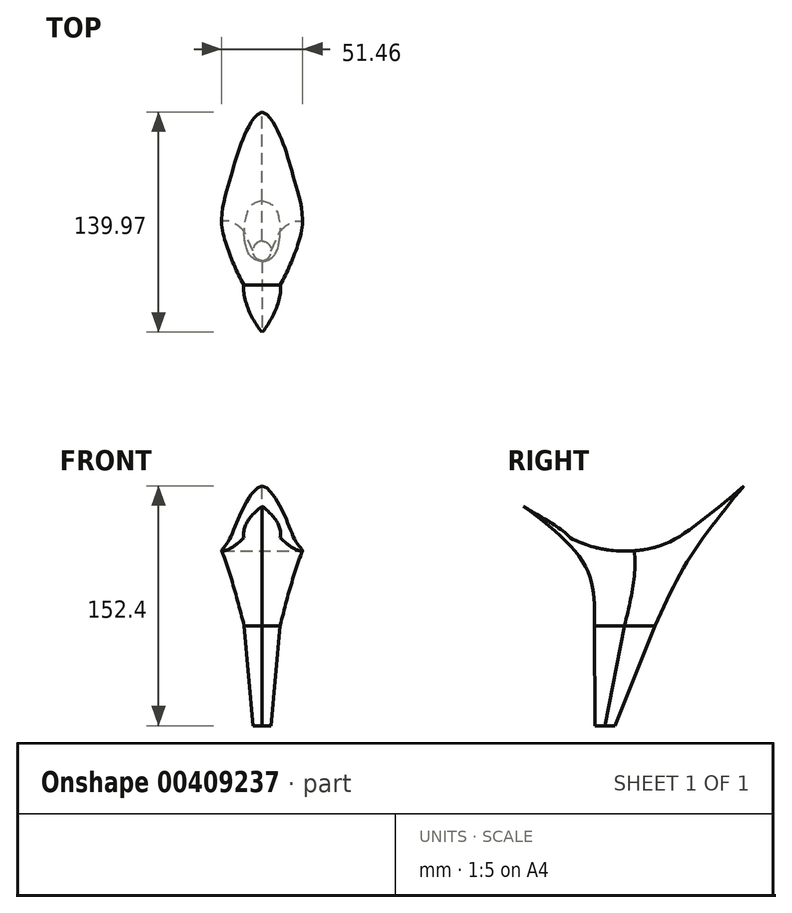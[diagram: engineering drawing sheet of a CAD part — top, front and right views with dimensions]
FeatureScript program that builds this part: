
annotation { "Feature Type Name" : "Feature", "Feature Type Description" : "" }
export const myFeature = defineFeature(function(context is Context, id is Id, definition is map)
    precondition{}
    {
        {
            var Q0;
            Q0=qCreatedBy(makeId("Top.planeOp"),FACE);
            var sketch = newSketch(context, id + "F0", { "sketchPlane" : qUnion([Q0])});
            skCircle(sketch, "E0", {"center": v(0, 0) * mm, "radius": 5.72 * mm, "construction": true});
            skFitSpline(sketch, "E1", {"points": [v(0, 6.35) * mm, v(-4.03, 4.38) * mm, v(-5.72, 0) * mm], "startDerivative": vector(-10.05, -1.39) * mm, "endDerivative": vector(-0.35, -12.15) * mm});
            skCircle(sketch, "E2", {"center": v(0, 0) * mm, "radius": 6.35 * mm, "construction": true});
            skFitSpline(sketch, "E3.MirrorCS", {"points": [v(0, 6.35) * mm, v(4.03, 4.38) * mm, v(5.72, 0) * mm], "startDerivative": vector(10.05, -1.39) * mm, "endDerivative": vector(0.35, -12.15) * mm});
            skFitSpline(sketch, "E4.MirrorCS", {"points": [v(0, -6.35) * mm, v(-4.03, -4.38) * mm, v(-5.72, 0) * mm], "startDerivative": vector(-10.05, 1.39) * mm, "endDerivative": vector(-0.35, 12.15) * mm});
            skFitSpline(sketch, "E5.MirrorCS", {"points": [v(0, -6.35) * mm, v(4.03, -4.38) * mm, v(5.72, 0) * mm], "startDerivative": vector(10.05, 1.39) * mm, "endDerivative": vector(0.35, 12.15) * mm});
            skSolve(sketch);
        }
        {
            var Q0;
            Q0=qCreatedBy(makeId("Top.planeOp"),FACE);
            cPlane(context, id + "F1", {"entities" : qUnion([Q0]), "cplaneType" : CPlaneType.OFFSET, "offset" : 63.5 * mm, "width" : 152.4 * mm, "height" : 152.4 * mm});
        }
        {
            var Q0;
            Q0=qCreatedBy(id+"F1.planeOp",FACE);
            var sketch = newSketch(context, id + "F2", { "sketchPlane" : qUnion([Q0])});
            skCircle(sketch, "E6", {"center": v(0, 12.7) * mm, "radius": 11.43 * mm, "construction": true});
            skCircle(sketch, "E7", {"center": v(0, 12.7) * mm, "radius": 19.05 * mm, "construction": true});
            skFitSpline(sketch, "E8", {"points": [v(0, 31.75) * mm, v(-8.42, 26.77) * mm, v(-11.43, 12.5) * mm], "startDerivative": vector(-23.54, -2.2) * mm, "endDerivative": vector(-0.5, -26.09) * mm});
            skFitSpline(sketch, "E9.MirrorCS", {"points": [v(0, 31.75) * mm, v(8.42, 26.77) * mm, v(11.43, 12.5) * mm], "startDerivative": vector(23.54, -2.2) * mm, "endDerivative": vector(0.5, -26.09) * mm});
            skLineSegment(sketch, "E10", {"start": v(-11.43, 12.5) * mm, "end": v(11.43, 12.5) * mm, "construction": true});
            skFitSpline(sketch, "E11.MirrorCS", {"points": [v(0, -6.74) * mm, v(-8.42, -1.77) * mm, v(-11.43, 12.5) * mm], "startDerivative": vector(-23.54, 2.2) * mm, "endDerivative": vector(-0.5, 26.09) * mm});
            skFitSpline(sketch, "E12.MirrorCS", {"points": [v(0, -6.74) * mm, v(8.42, -1.77) * mm, v(11.43, 12.5) * mm], "startDerivative": vector(23.54, 2.2) * mm, "endDerivative": vector(0.5, 26.09) * mm});
            skPoint(sketch, "E13.0", {"position": v(0, 0) * mm});
            skSolve(sketch);
        }
        {
            var Q0;
            Q0=makeQuery(id+"F0.imprint","IMPRINT",FACE,{"disambiguationData":[TD([[makeQuery(id+"F0.imprint","IMPRINT",EDGE,{"derivedFrom":sQuery(id+"F0.wireOp",EDGE,"E1")}),1.0]])]});
            var Q1;
            Q1=makeQuery(id+"F2.imprint","IMPRINT",FACE,{"disambiguationData":[TD([[makeQuery(id+"F2.imprint","IMPRINT",EDGE,{"derivedFrom":sQuery(id+"F2.wireOp",EDGE,"E8")}),1.0]])]});
            loft(context, id + "F3", {"sheetProfilesArray" : [{ "sheetProfileEntities" : qUnion([Q0]) }, { "sheetProfileEntities" : qUnion([Q1]) }]});
        }
        {
            var Q0;
            Q0=qCreatedBy(id+"F1.planeOp",FACE);
            cPlane(context, id + "F4", {"entities" : qUnion([Q0]), "cplaneType" : CPlaneType.OFFSET, "offset" : 38.1 * mm, "width" : 152.4 * mm, "height" : 152.4 * mm});
        }
        {
            var Q0;
            Q0=qCreatedBy(id+"F4.planeOp",FACE);
            var sketch = newSketch(context, id + "F5", { "sketchPlane" : qUnion([Q0])});
            skPoint(sketch, "E14.0", {"position": v(0, 0) * mm});
            skCircle(sketch, "E15", {"center": v(0, 19.05) * mm, "radius": 22.23 * mm, "construction": true});
            skCircle(sketch, "E16", {"center": v(0, 19.05) * mm, "radius": 31.75 * mm, "construction": true});
            skFitSpline(sketch, "E17", {"points": [v(0, 50.8) * mm, v(-14.15, 42.4) * mm, v(-22.22, 19.05) * mm], "startDerivative": vector(-46.14, -5.08) * mm, "endDerivative": vector(-0.3, -42.83) * mm});
            skLineSegment(sketch, "E18", {"start": v(-22.22, 19.05) * mm, "end": v(22.22, 19.05) * mm, "construction": true});
            skFitSpline(sketch, "E19.MirrorCS", {"points": [v(0, 50.8) * mm, v(14.15, 42.4) * mm, v(22.22, 19.05) * mm], "startDerivative": vector(46.14, -5.08) * mm, "endDerivative": vector(0.3, -42.83) * mm});
            skLineSegment(sketch, "E20.MirrorCS", {"start": v(22.22, 19.05) * mm, "end": v(-22.22, 19.05) * mm, "construction": true});
            skFitSpline(sketch, "E21.MirrorCS", {"points": [v(0, -12.7) * mm, v(-14.15, -4.3) * mm, v(-22.22, 19.05) * mm], "startDerivative": vector(-46.14, 5.08) * mm, "endDerivative": vector(-0.3, 42.83) * mm});
            skFitSpline(sketch, "E22.MirrorCS", {"points": [v(0, -12.7) * mm, v(14.15, -4.3) * mm, v(22.22, 19.05) * mm], "startDerivative": vector(46.14, 5.08) * mm, "endDerivative": vector(0.3, 42.83) * mm});
            skSolve(sketch);
        }
        {
            var Q0;
            Q0=qCreatedBy(id+"F4.planeOp",FACE);
            cPlane(context, id + "F6", {"entities" : qUnion([Q0]), "cplaneType" : CPlaneType.OFFSET, "offset" : 50.8 * mm, "width" : 152.4 * mm, "height" : 152.4 * mm});
        }
        {
            var Q0;
            Q0=qCreatedBy(id+"F6.planeOp",FACE);
            var sketch = newSketch(context, id + "F7", { "sketchPlane" : qUnion([Q0])});
            skPoint(sketch, "E23.0", {"position": v(0, 0) * mm});
            skCircle(sketch, "E24", {"center": v(0, 8.9) * mm, "radius": 44.45 * mm, "construction": true});
            skCircle(sketch, "E25", {"center": v(0, 8.9) * mm, "radius": 79.38 * mm, "construction": true});
            skFitSpline(sketch, "E26", {"points": [v(0, 88.26) * mm, v(-27.3, 62.72) * mm, v(-44.45, 8.9) * mm], "startDerivative": vector(-70.11, -4.65) * mm, "endDerivative": vector(4.08, -70.7) * mm});
            skLineSegment(sketch, "E27", {"start": v(-44.45, 8.9) * mm, "end": v(44.45, 8.9) * mm, "construction": true});
            skFitSpline(sketch, "E28.MirrorCS", {"points": [v(0, 88.26) * mm, v(27.3, 62.72) * mm, v(44.45, 8.9) * mm], "startDerivative": vector(70.11, -4.65) * mm, "endDerivative": vector(-4.08, -70.7) * mm});
            skFitSpline(sketch, "E29.MirrorCS", {"points": [v(0, -70.48) * mm, v(27.3, -44.94) * mm, v(44.45, 8.9) * mm], "startDerivative": vector(70.11, 4.65) * mm, "endDerivative": vector(-4.08, 70.7) * mm});
            skFitSpline(sketch, "E30.MirrorCS", {"points": [v(0, -70.48) * mm, v(-27.3, -44.94) * mm, v(-44.45, 8.9) * mm], "startDerivative": vector(-70.11, 4.65) * mm, "endDerivative": vector(4.08, 70.7) * mm});
            skSolve(sketch);
        }
        {
            var Q1;
            Q1=makeQuery(id+"F3.opLoft","CAP_FACE",FACE,{"disambiguationData":[OSD([makeQuery(id+"F2.imprint","IMPRINT",FACE,{"disambiguationData":[TD([[makeQuery(id+"F2.imprint","IMPRINT",EDGE,{"derivedFrom":sQuery(id+"F2.wireOp",EDGE,"E8")}),1.0]])]})])],"isStart":true});
            var Q2;
            Q2=makeQuery(id+"F5.imprint","IMPRINT",FACE,{"disambiguationData":[TD([[makeQuery(id+"F5.imprint","IMPRINT",EDGE,{"derivedFrom":sQuery(id+"F5.wireOp",EDGE,"E17")}),1.0]])]});
            var Q3;
            Q3=makeQuery(id+"F7.imprint","IMPRINT",FACE,{"disambiguationData":[TD([[makeQuery(id+"F7.imprint","IMPRINT",EDGE,{"derivedFrom":sQuery(id+"F7.wireOp",EDGE,"E26")}),1.0]])]});
            loft(context, id + "F8", {"sheetProfilesArray" : [{ "sheetProfileEntities" : qUnion([Q1]) }, { "sheetProfileEntities" : qUnion([Q2]) }, { "sheetProfileEntities" : qUnion([Q3]) }]});
        }
        {
            var Q0;
            Q0=qCreatedBy(makeId("Right.planeOp"),FACE);
            var sketch = newSketch(context, id + "F9", { "sketchPlane" : qUnion([Q0])});
            skFitSpline(sketch, "E31", {"points": [v(88.26, 152.4) * mm, v(61.41, 130.28) * mm, v(36.73, 114.88) * mm, v(2.95, 111.52) * mm, v(-33.09, 124.93) * mm], "startDerivative": vector(-132.87, -117.4) * mm, "endDerivative": vector(-161.22, 88.58) * mm});
            skFitSpline(sketch, "E32.0", {"points": [v(-12.7, 101.6) * mm, v(-22.23, 119.6) * mm, v(-46.36, 136) * mm, v(-70.48, 152.4) * mm]});
            skFitSpline(sketch, "E33.0.0", {"points": [v(12.5, 63.5) * mm, v(15.59, 76.45) * mm, v(18.68, 89.4) * mm, v(19.05, 101.6) * mm]});
            skFitSpline(sketch, "E33.0.1", {"points": [v(19.05, 101.6) * mm, v(19.6, 119.6) * mm, v(14.25, 136) * mm, v(8.9, 152.4) * mm]});
            skFitSpline(sketch, "E33.0.2", {"points": [v(8.9, 152.4) * mm, v(-17.57, 152.4) * mm, v(-44.03, 152.4) * mm, v(-70.48, 152.4) * mm]});
            skFitSpline(sketch, "E33.0.3", {"points": [v(-70.48, 152.4) * mm, v(-46.36, 136) * mm, v(-22.23, 119.6) * mm, v(-12.7, 101.6) * mm]});
            skFitSpline(sketch, "E34.0.2", {"points": [v(88.26, 152.4) * mm, v(61.8, 152.4) * mm, v(35.35, 152.4) * mm, v(8.9, 152.4) * mm]});
            skFitSpline(sketch, "E34.0.3", {"points": [v(8.89, 152.4) * mm, v(14.25, 136) * mm, v(19.6, 119.6) * mm, v(19.05, 101.6) * mm]});
            skFitSpline(sketch, "E34.0.4", {"points": [v(19.05, 101.6) * mm, v(18.68, 89.4) * mm, v(15.59, 76.45) * mm, v(12.5, 63.5) * mm]});
            skPoint(sketch, "E33.0.5.start.orphan", {"position": v(-6.74, 63.5) * mm});
            skPoint(sketch, "E34.0.0.start.orphan", {"position": v(31.75, 63.5) * mm});
            skPoint(sketch, "E34.0.1.start.orphan", {"position": v(50.8, 101.6) * mm});
            skPoint(sketch, "E35.orphan", {"position": v(-12.7, 101.6) * mm});
            skSolve(sketch);
        }
        {
            var Q0;
            Q0=qSketchRegion(id+"F9",true);
            extrude(context, id + "F10", {"entities" : qUnion([Q0]), "operationType" : NewBodyOperationType.REMOVE, "endBound" : BoundingType.THROUGH_ALL, "oppositeDirection" : true, "depth" : 25.4 * mm, "hasSecondDirection" : true, "secondDirectionBound" : SecondDirectionBoundingType.THROUGH_ALL, "secondDirectionOppositeDirection" : false, "secondDirectionDepth" : 25.4 * mm});
        }
        {
            var Q0;
            Q0=qSketchRegion(id+"F9",true);
            extrude(context, id + "F11", {"entities" : qUnion([Q0]), "operationType" : NewBodyOperationType.REMOVE, "endBound" : BoundingType.THROUGH_ALL, "oppositeDirection" : true, "depth" : 25.4 * mm, "hasSecondDirection" : true, "secondDirectionBound" : SecondDirectionBoundingType.THROUGH_ALL, "secondDirectionOppositeDirection" : false, "secondDirectionDepth" : 25.4 * mm});
        }
    });
